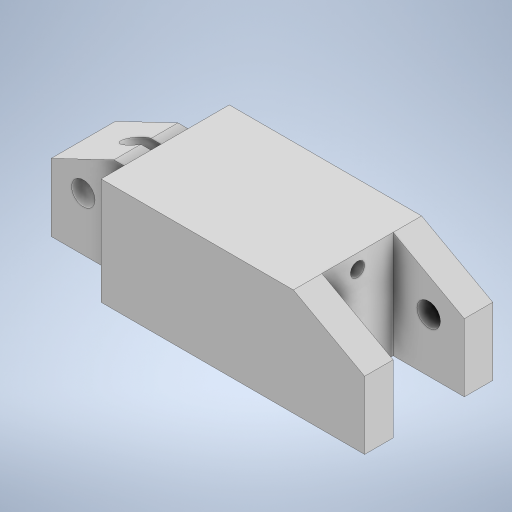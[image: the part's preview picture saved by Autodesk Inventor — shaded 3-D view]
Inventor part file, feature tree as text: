
AUTODESK INVENTOR PART (.ipt)
format: ipt  version: 2024 (Build 280153000, 153)  size: 473,088 bytes
history: native  units: mm
features: sketch x27, extrude x22, plane x5, chamfer x3, move_body x3, split x2, boolean_combine x2
ambient origin geometry x8: Origin, YZ Plane, XZ Plane, XY Plane, X Axis, Y Axis, Z Axis, Center Point
bodies: Solid1 (feature_tree), Solid2 (feature_tree), Solid3 (feature_tree), Solid4 (feature_tree), Solid5 (feature_tree)
feature tree (64):
  extrude  "Extrusion1"  Depth=16.0mm
  sketch  "Sketch2"  dims[d2=15.0mm d3=0.0mm d4=10.0mm]
  extrude  "Extrusion2"  Depth=10.0mm
  chamfer  "Chamfer1"  Distance=21.25mm
  extrude  "Extrusion3"  Depth=10.0mm TaperAngle=0.0deg
  extrude  "Extrusion4"  Depth=11.5mm TaperAngle=0.0deg
  extrude  "Extrusion5"  Depth=1.0mm TaperAngle=0.0deg
  chamfer  "Chamfer2"  Distance=6.0mm Angle=45.0deg
  sketch  "Sketch6"  dims[d14=7.0mm d15=11.5mm d16=0.0mm]
  extrude  "Extrusion6"  Depth=9.0mm
  extrude  "Extrusion7"  Depth=11.5mm TaperAngle=0.0deg
  chamfer  "Chamfer3"  Distance=11.5mm Angle=45.0deg
  sketch  "Sketch9"  dims[d26=3.3mm d27=45.25mm d28=0.0mm d29=11.5mm d30=5.5mm d31=45.0deg]
  extrude  "Extrusion8"  Depth=65.75mm TaperAngle=0.0deg
  extrude  "Extrusion9"  Depth=9.0mm TaperAngle=0.0deg
  extrude  "Extrusion10"  Depth=13.0mm TaperAngle=0.0deg
  sketch  "Sketch13"  dims[d43=24.0mm d44=21.0mm d45=0.0mm]
  extrude  "Extrusion11"  Depth=21.0mm TaperAngle=0.0deg
  extrude  "Extrusion12"  TaperAngle=0.0deg  [1 undecoded]
  extrude  "Extrusion13"  Depth=6.0mm TaperAngle=0.0deg
  plane  "Work Plane1"
  split  "Split1"
  move_body  "Move Body1"
  extrude  "Extrusion14"  Depth=0.5mm TaperAngle=0.0deg
  move_body  "Move Body2"
  extrude  "Extrusion15"  Depth=3.0mm
  sketch  "Sketch19"  dims[d70=31.0mm d71=29.5mm d72=0.0mm]
  sketch  "Sketch20"  dims[d76=-5.0mm d77=0.0mm d78=0.0mm d95=26.0mm d96=0.0mm]
  extrude  "Extrusion16"  Depth=1.0mm
  extrude  "Extrusion18"  Depth=29.5mm TaperAngle=0.0deg
  extrude  "Extrusion19"  Depth=26.0mm TaperAngle=0.0deg
  plane  "Work Plane5"
  sketch  "Sketch23"
  plane  "Work Plane7"
  sketch  "Sketch24"
  extrude  "Extrusion20"  Depth=1.0mm TaperAngle=0.0deg
  plane  "Work Plane2"
  boolean_combine  "Combine1"
  split  "Split2"
  plane  "Work Plane6"
  move_body  "Move Body3"
  boolean_combine  "Combine2"
  extrude  "Extrusion27"  [1 undecoded]
  sketch  "Sketch33"
  extrude  "Extrusion28"  [1 undecoded]
  extrude  "Extrusion29"  [1 undecoded]
  sketch  "Sketch1"  dims[d0=36.0mm d1=16.0mm]
  sketch  "Sketch3"  dims[d5=10.0mm]
  sketch  "Sketch4"  dims[d6=3.3mm d7=21.25mm d8=0.0mm]
  sketch  "Sketch5"  dims[d9=10.0mm d10=5.5mm d11=45.0deg d12=10.0mm d13=0.0mm]
  sketch  "Sketch7"  dims[d17=3.3mm d18=1.0mm d19=0.0mm d20=6.0mm d21=11.5mm d22=45.0deg]
  sketch  "Sketch8"  dims[d23=15.0mm d24=0.0mm d25=9.0mm]
  sketch  "Sketch10"  dims[d32=2.0mm d33=65.75mm d34=0.0mm]
  sketch  "Sketch11"  dims[d35=0.5mm d36=0.0mm d37=9.0mm d38=0.0mm]
  sketch  "Sketch12"  dims[d39=0.5mm d40=0.0mm d41=13.0mm d42=0.0mm]
  sketch  "Sketch14"  dims[d46=12.25mm d47=-12.0mm d48=0.0mm d49=0.0mm]
  sketch  "Sketch15"  dims[d50=30.0mm d51=0.0mm d52=6.0mm d53=0.0mm d54=0.0mm]
  sketch  "Sketch16"  dims[d56=0.5mm d57=0.0mm d58=0.5mm d59=0.0mm]
  sketch  "Sketch17"  dims[d64=10.0mm d65=0.0mm d66=3.0mm]
  sketch  "Sketch18"  dims[d67=10.0mm d68=0.0mm d69=1.0mm]
  sketch  "Sketch22"  dims[d97=1.0mm d98=0.0mm d99=1.0mm d100=0.0mm]
  sketch  "Sketch25"
  sketch  "Sketch32"
  sketch  "Sketch34"
note: 4 required parameter values undecoded (feature->parameter linkage not recoverable at this tier; creation-order binding heuristic only, values carry confidence <= 0.55)
